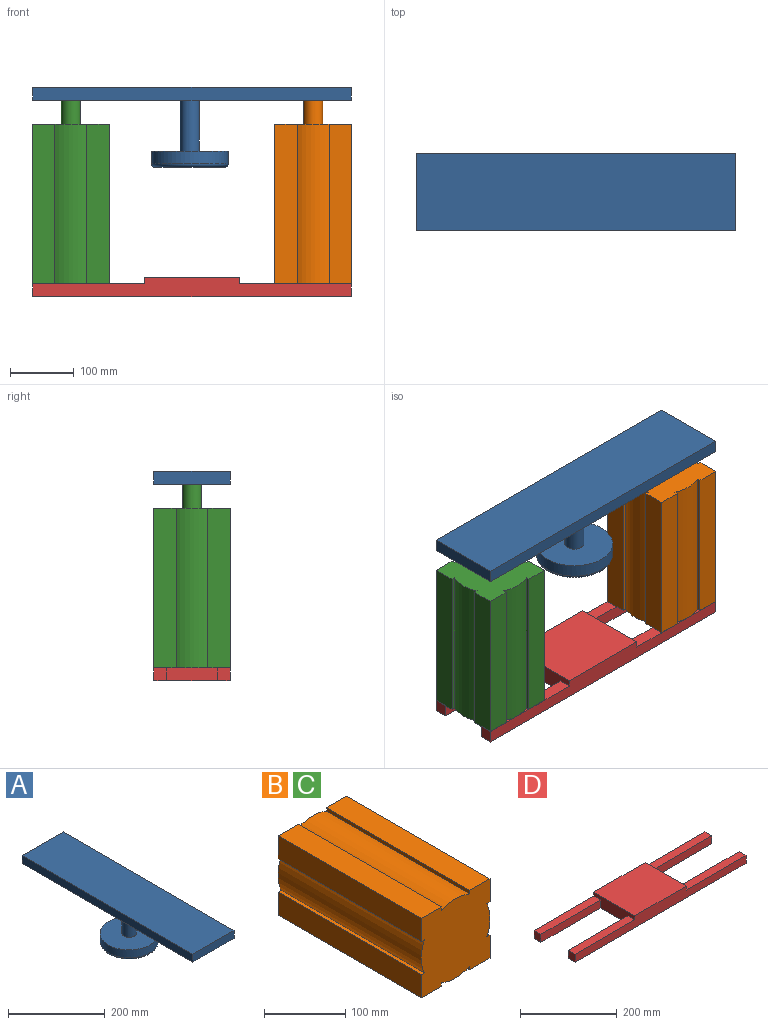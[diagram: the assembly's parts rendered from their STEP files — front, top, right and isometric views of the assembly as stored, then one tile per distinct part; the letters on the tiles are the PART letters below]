
ASSEMBLY  parts=4 mates=9
PART A: 11 faces, bbox 129.9x500x125 mm
  f0: plane 120x20mm, normal (0,1,0), area 2400mm2, adj f1,f3,f4,f5
  f1: plane 500x20mm, normal (-1,0,0), area 10000mm2, adj f0,f2,f4,f5
  f2: plane 120x20mm, normal (0,-1,0), area 2400mm2, adj f1,f3,f4,f5
  f3: plane 500x20mm, normal (1,0,0), area 10000mm2, adj f0,f2,f4,f5
  f4: plane 500x120mm, normal (0,0,1), area 60000mm2, adj f0,f1,f2,f3
  f5: plane 500x120mm, normal (0,0,-1), area 59293.1mm2, adj f0,f1,f2,f3,f6
  f6: cylinder r=15mm len=80mm, axis (0,0,1), area 7539.8mm2, adj f5,f9
  f7: cylinder r=60mm len=120mm, axis (0,0,1), area 7539.8mm2, adj f9,f10
  f8: plane 110x110mm, normal (0,0,-1), area 9503.3mm2, adj f10
  f9: plane 120x120mm, normal (0,0,1), area 10602.9mm2, adj f6,f7
  f10: torus R=55mm, axis (0,0,-1), area 2871.2mm2, adj f7,f8
PART B: 24 faces, bbox 120x288x120 mm
  f0: plane 250x35mm, normal (0,0,-1), area 8750mm2, adj f1,f19,f20,f21
  f1: plane 250x35mm, normal (1,0,0), area 8750mm2, adj f0,f2,f20,f21
  f2: plane 250x5.46mm, normal (0,0,1), area 1364.1mm2, adj f1,f3,f20,f21
  f3: cylinder r=60mm len=250mm, axis (0,1,0), area 12893.3mm2, adj f2,f4,f20,f21
  f4: plane 250x5.46mm, normal (0,0,-1), area 1364.1mm2, adj f3,f5,f20,f21
  f5: plane 250x35mm, normal (1,0,0), area 8750mm2, adj f4,f6,f20,f21
  f6: plane 250x35mm, normal (0,0,1), area 8750mm2, adj f5,f7,f20,f21
  f7: plane 250x5.46mm, normal (-1,0,0), area 1364.1mm2, adj f6,f8,f20,f21
  f8: cylinder r=60mm len=250mm, axis (0,1,0), area 12893.3mm2, adj f7,f9,f20,f21
  f9: plane 250x5.46mm, normal (1,0,0), area 1364.1mm2, adj f8,f10,f20,f21
  f10: plane 250x35mm, normal (0,0,1), area 8750mm2, adj f9,f11,f20,f21
  f11: plane 250x35mm, normal (-1,0,0), area 8750mm2, adj f10,f12,f20,f21
  f12: plane 250x5.46mm, normal (0,0,-1), area 1364.1mm2, adj f11,f13,f20,f21
  f13: cylinder r=60mm len=250mm, axis (0,1,0), area 12893.3mm2, adj f12,f14,f20,f21
  f14: plane 250x5.46mm, normal (0,0,1), area 1364.1mm2, adj f13,f15,f20,f21
  f15: plane 250x35mm, normal (-1,0,0), area 8750mm2, adj f14,f16,f20,f21
  f16: plane 250x35mm, normal (0,0,-1), area 8750mm2, adj f15,f17,f20,f21
  f17: plane 250x5.46mm, normal (1,0,0), area 1364.1mm2, adj f16,f18,f20,f21
  f18: cylinder r=60mm len=250mm, axis (0,1,0), area 12893.3mm2, adj f17,f19,f20,f21
  f19: plane 250x5.46mm, normal (-1,0,0), area 1364.1mm2, adj f0,f18,f20,f21
  f20: plane 120x120mm, normal (0,-1,0), area 14043.1mm2, adj f0,f1,f2,f3,f4,f5,f6,f7
  f21: plane 120x120mm, normal (0,1,0), area 13336.3mm2, adj f0,f1,f2,f3,f4,f5,f6,f7
  f22: cylinder r=15mm len=38mm, axis (0,-1,0), area 3581.4mm2, adj f21,f23
  f23: plane 30x30mm, normal (0,1,0), area 706.9mm2, adj f22
PART C: same geometry as B
PART D: 18 faces, bbox 500x120x30 mm
  f0: plane 175x20mm, normal (0,0,1), area 3500mm2, adj f5,f6,f7,f8
  f1: plane 175x20mm, normal (0,0,1), area 3500mm2, adj f3,f4,f5,f14
  f2: plane 175x20mm, normal (0,0,1), area 3500mm2, adj f8,f9,f10,f11
  f3: plane 20x20mm, normal (-1,0,0), area 400mm2, adj f1,f4,f14,f16
  f4: plane 175x20mm, normal (0,-1,0), area 3500mm2, adj f1,f3,f5,f16
  f5: plane 120x30mm, normal (-1,0,0), area 2800mm2, adj f0,f1,f4,f6,f8,f14,f16,f17
  f6: plane 175x20mm, normal (0,1,0), area 3500mm2, adj f0,f5,f7,f16
  f7: plane 20x20mm, normal (-1,0,0), area 400mm2, adj f0,f6,f8,f16
  f8: plane 500x30mm, normal (0,-1,0), area 11500mm2, adj f0,f2,f5,f7,f9,f11,f16,f17
  f9: plane 20x20mm, normal (1,0,0), area 400mm2, adj f2,f8,f10,f16
  f10: plane 175x20mm, normal (0,1,0), area 3500mm2, adj f2,f9,f11,f16
  f11: plane 120x30mm, normal (1,0,0), area 2800mm2, adj f2,f8,f10,f12,f14,f15,f16,f17
  f12: plane 175x20mm, normal (0,-1,0), area 3500mm2, adj f11,f13,f15,f16
  f13: plane 20x20mm, normal (1,0,0), area 400mm2, adj f12,f14,f15,f16
  f14: plane 500x30mm, normal (0,1,0), area 11500mm2, adj f1,f3,f5,f11,f13,f15,f16,f17
  f15: plane 175x20mm, normal (0,0,1), area 3500mm2, adj f11,f12,f13,f14
  f16: plane 500x120mm, normal (0,0,-1), area 32000mm2, adj f3,f4,f5,f6,f7,f8,f9,f10
  f17: plane 150x120mm, normal (0,0,1), area 18000mm2, adj f5,f8,f11,f14
PLACE A rot(axis=(0,0,-1),90deg) t=(19.74,-759.15,404.15)mm
PLACE B rot(axis=(1,0,0),90deg) t=(209.74,-759.15,366.15)mm
PLACE C rot(axis=(0,-0.71,-0.71),180deg) t=(-170.26,-759.15,366.15)mm
PLACE D t=(19.74,-759.15,96.15)mm
MATE planar D.f8 <-> B.f6  axis (0,-1,0) through (269.74,-819.15,106.15)mm
MATE planar A.f1 <-> C.f6  axis (0,1,0) through (-230.26,-699.15,424.15)mm
MATE planar D.f0 <-> C.f3  axis (0,0,1) through (-142.76,-809.15,116.15)mm
MATE planar C.f3 <-> B.f3  axis (0,0,-1) through (-170.26,-759.15,116.15)mm
MATE planar B.f0 <-> C.f6  axis (0,1,0) through (252.24,-699.15,241.15)mm
MATE planar A.f5 <-> C.f3  axis (0,0,-1) through (19.78,-759.15,404.15)mm
MATE planar B.f5 <-> D.f9  axis (1,0,0) through (269.74,-801.65,241.15)mm
MATE planar C.f1 <-> A.f2  axis (-1,0,0) through (-230.26,-801.65,241.15)mm
MATE planar D.f3 <-> C.f5  axis (-1,0,0) through (-230.26,-709.15,106.15)mm
